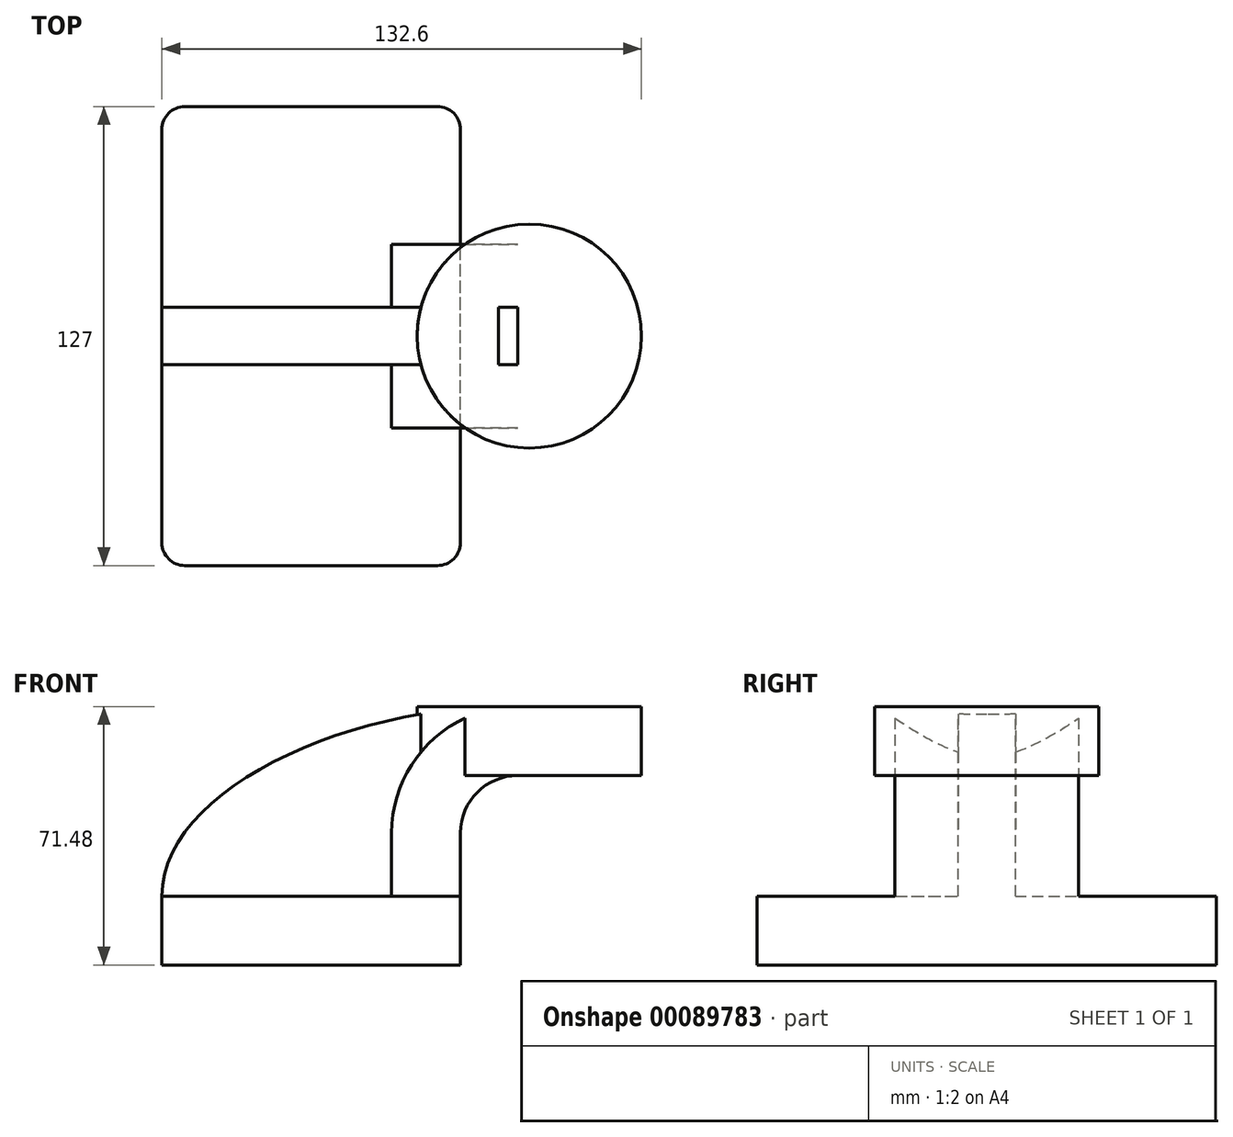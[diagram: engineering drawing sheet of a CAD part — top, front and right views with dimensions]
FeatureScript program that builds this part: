
annotation { "Feature Type Name" : "Feature", "Feature Type Description" : "" }
export const myFeature = defineFeature(function(context is Context, id is Id, definition is map)
    precondition{}
    {
        {
            var Q0;
            Q0=qCreatedBy(makeId("Front.planeOp"),FACE);
            var sketch = newSketch(context, id + "F0", { "sketchPlane" : qUnion([Q0])});
            skLineSegment(sketch, "E0.bottom", {"start": v(41.28, -9.52) * mm, "end": v(-41.28, -9.53) * mm});
            skLineSegment(sketch, "E0.top", {"start": v(41.27, 9.53) * mm, "end": v(-41.28, 9.52) * mm});
            skLineSegment(sketch, "E0.left", {"start": v(41.28, -9.52) * mm, "end": v(41.28, 9.53) * mm});
            skLineSegment(sketch, "E0.right", {"start": v(-41.27, -9.52) * mm, "end": v(-41.28, 9.52) * mm});
            skPoint(sketch, "E0.middle", {"position": v(0, 0) * mm});
            skLineSegment(sketch, "E1.bottom", {"start": v(111.12, 38.1) * mm, "end": v(60.32, 38.1) * mm});
            skLineSegment(sketch, "E1.top", {"start": v(111.12, 66.68) * mm, "end": v(60.32, 66.68) * mm});
            skLineSegment(sketch, "E1.left", {"start": v(111.12, 38.1) * mm, "end": v(111.12, 66.68) * mm});
            skLineSegment(sketch, "E1.right", {"start": v(60.32, 38.1) * mm, "end": v(60.32, 66.68) * mm});
            skPoint(sketch, "E1.middle", {"position": v(85.72, 52.39) * mm});
            skLineSegment(sketch, "E2", {"start": v(41.27, 9.53) * mm, "end": v(41.27, 27) * mm});
            skArc(sketch, "E3", {"start": v(41.27, 27) * mm, "mid": v(45.92, 38.23) * mm, "end": v(57.15, 42.88) * mm});
            skLineSegment(sketch, "E4", {"start": v(57.15, 42.88) * mm, "end": v(91.32, 42.88) * mm});
            skLineSegment(sketch, "E5.0", {"start": v(57.15, 61.93) * mm, "end": v(91.32, 61.93) * mm});
            skArc(sketch, "E5.1", {"start": v(22.22, 27) * mm, "mid": v(32.45, 51.7) * mm, "end": v(57.15, 61.93) * mm});
            skLineSegment(sketch, "E5.2", {"start": v(22.22, 9.53) * mm, "end": v(22.22, 27) * mm});
            skLineSegment(sketch, "E6", {"start": v(41.27, 9.53) * mm, "end": v(22.22, 9.53) * mm});
            skFitSpline(sketch, "E7", {"points": [v(-41.28, 9.53) * mm, v(57.15, 61.93) * mm], "startDerivative": vector(-0.5, 87.8) * mm, "endDerivative": vector(139.82, -2.87) * mm});
            skLineSegment(sketch, "E8", {"start": v(91.32, 38.1) * mm, "end": v(91.32, 66.68) * mm});
            skSolve(sketch);
        }
        {
            var Q0;
            Q0=makeQuery(id+"F0.imprint","IMPRINT",FACE,{"disambiguationData":[TD([[makeQuery(id+"F0.imprint","IMPRINT",EDGE,{"derivedFrom":sQuery(id+"F0.wireOp",EDGE,"E0.bottom")}),-1.0]])]});
            extrude(context, id + "F1", {"entities" : qUnion([Q0]), "endBound" : BoundingType.SYMMETRIC, "depth" : 127 * mm});
        }
        {
            var Q0;
            {var subQ5=sQuery(id+"F0.wireOp",EDGE,"Lg36pwPp-ddmd-6lvj-Lo5e-NaX46Flrr5Re");Q0=makeQuery(id+"F0.imprint","IMPRINT",FACE,{"disambiguationData":[TD([[makeQuery(id+"F0.imprint","IMPRINT",EDGE,{"derivedFrom":subQ5}),-1.0]])]});}
            var Q1;
            Q1=makeQuery(id+"F0.imprint","IMPRINT",FACE,{"disambiguationData":[TD([[makeQuery(id+"F0.imprint","IMPRINT",EDGE,{"derivedFrom":sQuery(id+"F0.wireOp",EDGE,"E2")}),1.0]])]});
            extrude(context, id + "F2", {"entities" : qUnion([Q0, Q1]), "operationType" : NewBodyOperationType.ADD, "endBound" : BoundingType.SYMMETRIC, "depth" : 50.8 * mm});
        }
        {
            var Q0;
            Q0=makeQuery(id+"F0.imprint","IMPRINT",FACE,{"disambiguationData":[TD([[makeQuery(id+"F0.imprint","IMPRINT",EDGE,{"derivedFrom":sQuery(id+"F0.wireOp",EDGE,"E0.top")}),-1.0]])]});
            extrude(context, id + "F3", {"entities" : qUnion([Q0]), "operationType" : NewBodyOperationType.ADD, "endBound" : BoundingType.SYMMETRIC, "depth" : 15.88 * mm});
        }
        {
            var Q0;
            {var subQ0=sQuery(id+"F0.wireOp",EDGE,"E4");var subQ1=sQuery(id+"F0.wireOp",EDGE,"E1.right");var subQ2=makeQuery(id+"F0.imprint","INTERSECT",VERTEX,{"derivedFrom":[subQ1,subQ0]});Q0=makeQuery(id+"F0.imprint","IMPRINT",FACE,{"disambiguationData":[TD([[makeQuery(id+"F0.imprint","IMPRINT",EDGE,{"disambiguationData":[TD([[subQ2,-1.0]])],"derivedFrom":subQ1}),-1.0]])]});}
            var Q1;
            Q1=sQuery(id+"F0.wireOp",EDGE,"E1.right");
            revolve(context, id + "F4", {"operationType" : NewBodyOperationType.ADD, "entities" : qUnion([Q0]), "axis" : qUnion([Q1]), "revolveType" : RevolveType.FULL});
        }
        {
            var Q0;
            Q0=makeQuery(id+"F1.opExtrude","CAP_EDGE",EDGE,{"disambiguationData":[OSD([sQuery(id+"F0.wireOp",EDGE,"E0.left")])],"isStart":false});
            var Q1;
            Q1=makeQuery(id+"F1.opExtrude","CAP_EDGE",EDGE,{"disambiguationData":[OSD([sQuery(id+"F0.wireOp",EDGE,"E0.right")])],"isStart":false});
            var Q2;
            Q2=makeQuery(id+"F1.opExtrude","CAP_EDGE",EDGE,{"disambiguationData":[OSD([sQuery(id+"F0.wireOp",EDGE,"E0.left")])],"isStart":true});
            var Q3;
            Q3=makeQuery(id+"F1.opExtrude","CAP_EDGE",EDGE,{"disambiguationData":[OSD([sQuery(id+"F0.wireOp",EDGE,"E0.right")])],"isStart":true});
            fillet(context, id + "F5", {"entities" : qUnion([Q0, Q1, Q2, Q3]), "radius" : 6.35 * mm, "tangentPropagation" : true, "allowEdgeOverflow" : false});
        }
    });
